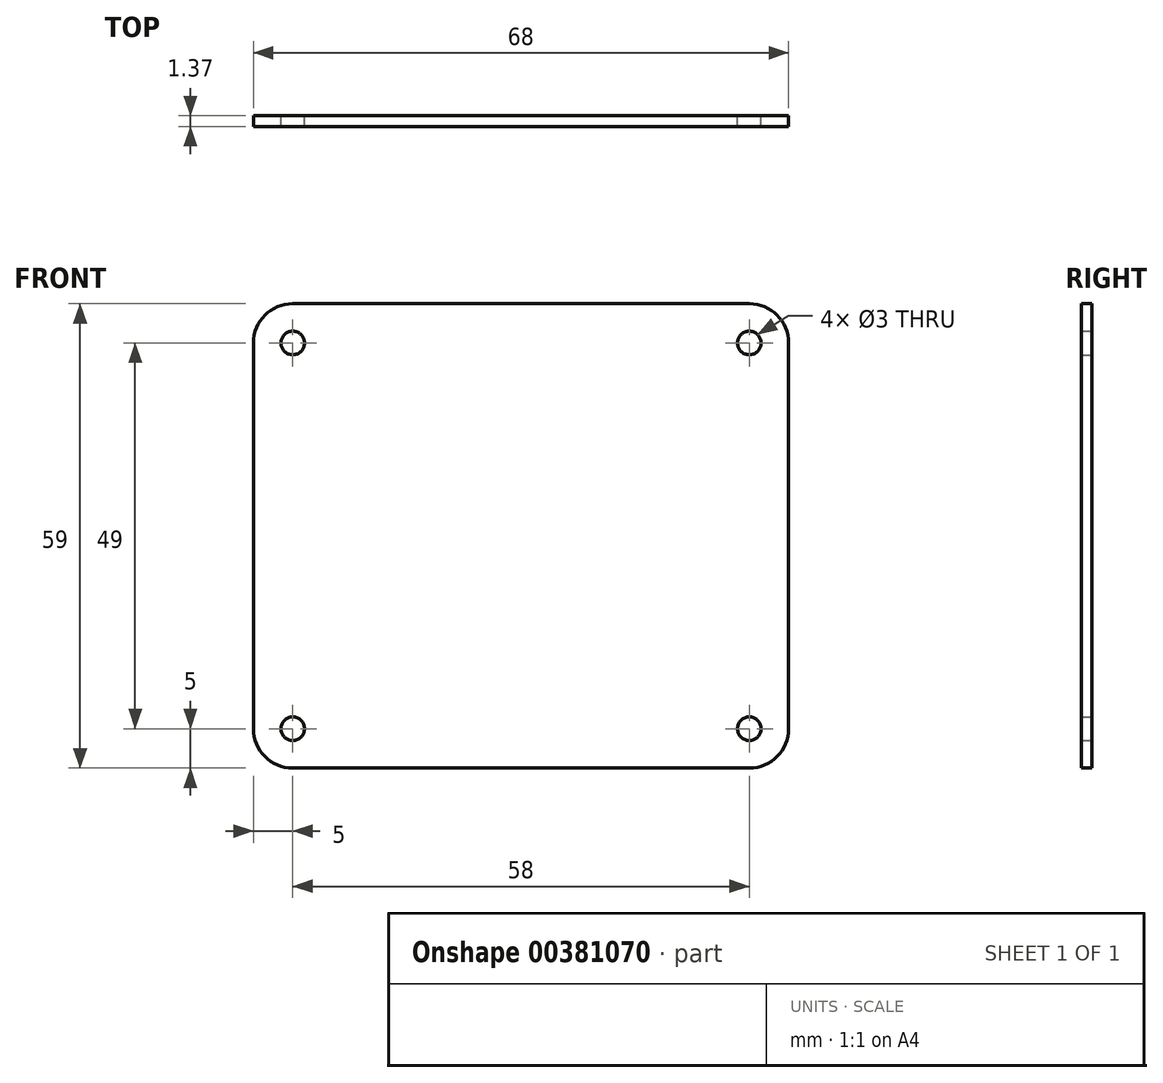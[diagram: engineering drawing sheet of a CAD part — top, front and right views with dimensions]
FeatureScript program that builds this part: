
annotation { "Feature Type Name" : "Feature", "Feature Type Description" : "" }
export const myFeature = defineFeature(function(context is Context, id is Id, definition is map)
    precondition{}
    {
        {
            var Q0;
            Q0=qCreatedBy(makeId("Front.planeOp"),FACE);
            var sketch = newSketch(context, id + "F0", { "sketchPlane" : qUnion([Q0])});
            skPoint(sketch, "E0.middle", {"position": v(0, 0) * mm});
            skLineSegment(sketch, "E1.bottom", {"start": v(29, 24.5) * mm, "end": v(-29, 24.5) * mm});
            skLineSegment(sketch, "E1.top", {"start": v(29, -24.5) * mm, "end": v(-29, -24.5) * mm});
            skLineSegment(sketch, "E1.left", {"start": v(29, 24.5) * mm, "end": v(29, -24.5) * mm});
            skLineSegment(sketch, "E1.right", {"start": v(-29, 24.5) * mm, "end": v(-29, -24.5) * mm});
            skCircle(sketch, "E2", {"center": v(-29, 24.5) * mm, "radius": 1.5 * mm});
            skCircle(sketch, "E3", {"center": v(29, 24.5) * mm, "radius": 1.5 * mm});
            skCircle(sketch, "E4", {"center": v(29, -24.5) * mm, "radius": 1.5 * mm});
            skCircle(sketch, "E5", {"center": v(-29, -24.5) * mm, "radius": 1.5 * mm});
            skLineSegment(sketch, "E6", {"start": v(-29, 24.5) * mm, "end": v(-34, 29.5) * mm, "construction": true});
            skLineSegment(sketch, "E7", {"start": v(-34, 29.5) * mm, "end": v(-29, 29.5) * mm, "construction": true});
            skLineSegment(sketch, "E8", {"start": v(-29, 29.5) * mm, "end": v(-29, 24.5) * mm, "construction": true});
            skLineSegment(sketch, "E9", {"start": v(29, -24.5) * mm, "end": v(34, -29.5) * mm, "construction": true});
            skLineSegment(sketch, "E10", {"start": v(34, -29.5) * mm, "end": v(29, -29.5) * mm, "construction": true});
            skLineSegment(sketch, "E11", {"start": v(29, -29.5) * mm, "end": v(29, -24.5) * mm, "construction": true});
            skLineSegment(sketch, "E12.bottom", {"start": v(-29, 29.5) * mm, "end": v(29, 29.5) * mm});
            skLineSegment(sketch, "E12.top", {"start": v(-29, -29.5) * mm, "end": v(29, -29.5) * mm});
            skLineSegment(sketch, "E12.left", {"start": v(-34, 24.5) * mm, "end": v(-34, -24.5) * mm});
            skLineSegment(sketch, "E12.right", {"start": v(34, 24.5) * mm, "end": v(34, -24.5) * mm});
            skPoint(sketch, "E13.visualSharp", {"position": v(-34, 29.5) * mm});
            skArc(sketch, "E13.filletArc", {"start": v(-29, 29.5) * mm, "mid": v(-32.54, 28.04) * mm, "end": v(-34, 24.5) * mm});
            skPoint(sketch, "E14.visualSharp", {"position": v(34, 29.5) * mm});
            skArc(sketch, "E14.filletArc", {"start": v(34, 24.5) * mm, "mid": v(32.54, 28.04) * mm, "end": v(29, 29.5) * mm});
            skPoint(sketch, "E15.visualSharp", {"position": v(34, -29.5) * mm});
            skArc(sketch, "E15.filletArc", {"start": v(29, -29.5) * mm, "mid": v(32.54, -28.04) * mm, "end": v(34, -24.5) * mm});
            skPoint(sketch, "E16.visualSharp", {"position": v(-34, -29.5) * mm});
            skArc(sketch, "E16.filletArc", {"start": v(-34, -24.5) * mm, "mid": v(-32.54, -28.04) * mm, "end": v(-29, -29.5) * mm});
            skSolve(sketch);
        }
        {
            var Q0;
            Q0 = qSketchRegion(id + "F0", true);
            var Q1;
            {var subQ5=sQuery(id+"F0.wireOp",EDGE,"E3");var subQ13=sQuery(id+"F0.wireOp",EDGE,"E1.bottom");var subQ14=makeQuery(id+"F0.imprint","INTERSECT",VERTEX,{"derivedFrom":[subQ13,subQ5]});Q1=makeQuery(id+"F0.imprint","IMPRINT",FACE,{"disambiguationData":[TD([[makeQuery(id+"F0.imprint","IMPRINT",EDGE,{"disambiguationData":[TD([[subQ14,-1.0]])],"derivedFrom":subQ13}),1.0]])]});}
            extrude(context, id + "F1", {"entities" : qUnion([Q0, Q1]), "depth" : 1.37 * mm});
        }
    });
